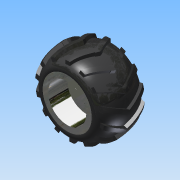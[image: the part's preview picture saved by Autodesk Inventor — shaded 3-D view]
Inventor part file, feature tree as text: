
AUTODESK INVENTOR PART (.ipt)
format: ipt  version: 2014 (Build 180170000, 170)  size: 1,057,792 bytes
history: native  units: in
note: dims shown in document units (in); Inventor stores cm internally (conversion verified against a paired STEP export)
features: sketch x10, extrude x8, projected_geometry x3, revolve x2, plane x2, mirror x2, pattern_circular x1
ambient origin geometry x8: Origin, YZ Plane, XZ Plane, XY Plane, X Axis, Y Axis, Z Axis, Center Point
bodies: Solid1 (feature_tree)
feature tree (28):
  extrude  "Extrusion1"  Depth=2.84in
  extrude  "Extrusion2"  Depth=0.326in TaperAngle=0.0deg
  extrude  "Extrusion3"  Depth=0.15in
  extrude  "Extrusion4"  Depth=2.6in
  extrude  "Extrusion5"  Depth=0.3in
  extrude  "Extrusion6"  Depth=1.33in
  revolve  "Revolution1"  [1 undecoded]
  extrude  "Extrusion7"  Depth=1.1811in TaperAngle=360.0deg
  plane  "Work Plane1"
  plane  "Work Plane2"
  extrude  "Extrusion8"  Depth=0.26in
  mirror  "Mirror3"
  pattern_circular  "Circular Pattern2"  [2 undecoded]
  revolve  "Revolution3"  Angle=90.0deg
  mirror  "Mirror4"
  sketch  "Sketch1"  dims[d0=2.6in d1=2.84in]
  sketch  "Sketch2"  dims[d2=1.48in d3=0.0in d4=0.326in d5=0.0in]
  sketch  "Sketch3"  dims[d6=0.824in d7=0.15in]
  sketch  "Sketch4"  dims[d8=0.31in d9=0.0in d10=2.6in]
  sketch  "Sketch5"  dims[d11=1.314in d12=0.0in d13=0.3in]
  sketch  "Sketch6"  dims[d14=0.41in d15=0.0in d16=1.33in]
  sketch  "Sketch7"  dims[d17=0.05in d18=0.05in]
  sketch  "Sketch8"  dims[d19=0.025in d20=1.1811in d22=360.0deg]
  sketch  "Sketch9"  dims[d24=0.32in d25=0.0in d26=0.26in]
  sketch  "Sketch11"  dims[d27=0.26in d31=5.0in d32=90.0deg d33=0.375in d34=0.6575in d35=3.1496in d37=360.0deg d39=0.21in d40=0.0in d41=2.7in d49=1.0in d50=0.0in d54=-1.56in d56=0.4323in d57=0.4368in d58=0.4641in d59=0.165in d60=1.5732in d61=1.815in d62=0.21in d63=0.3422in d64=0.0555in d65=1.5412in d66=0.8691in d67=1.5732in d68=0.1336in d69=5.5118in d70=360.0deg d72=90.0deg d73=2.7863in]
  projected_geometry  "Project Cut Edges1"
  projected_geometry  "Project Cut Edges2"
  projected_geometry  "Project Cut Edges3"
note: 3 required parameter values undecoded (feature->parameter linkage not recoverable at this tier; creation-order binding heuristic only, values carry confidence <= 0.55)